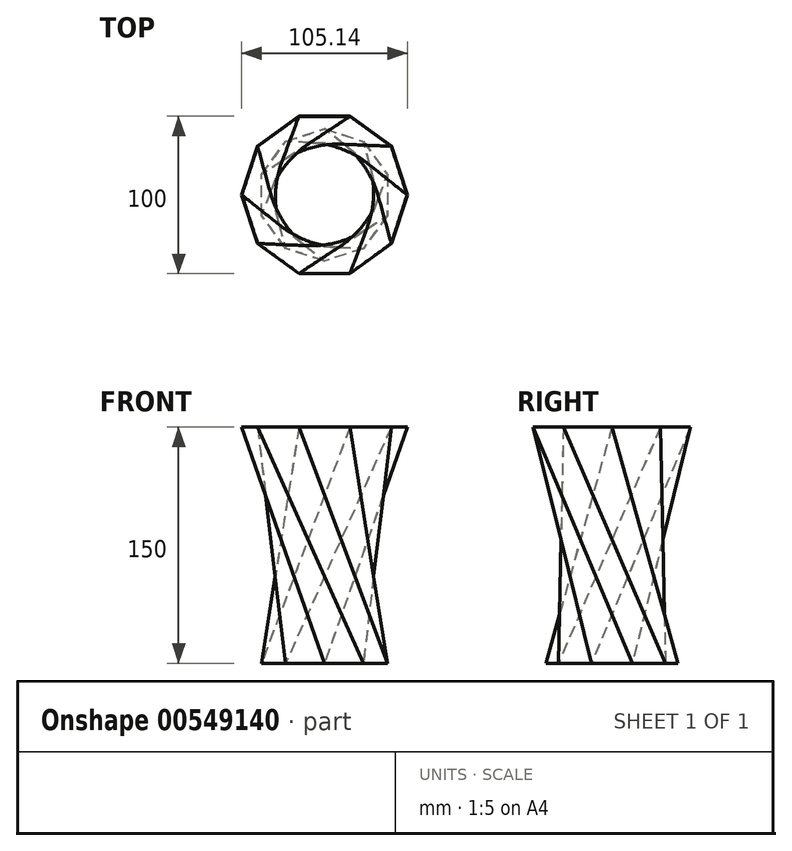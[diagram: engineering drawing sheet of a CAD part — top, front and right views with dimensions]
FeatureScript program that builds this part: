
annotation { "Feature Type Name" : "Feature", "Feature Type Description" : "" }
export const myFeature = defineFeature(function(context is Context, id is Id, definition is map)
    precondition{}
    {
        {
            var Q0;
            Q0=qCreatedBy(makeId("Top.planeOp"),FACE);
            var sketch = newSketch(context, id + "F0", { "sketchPlane" : qUnion([Q0])});
            skCircle(sketch, "E0.cCircle", {"center": v(0, 0) * mm, "radius": 40 * mm, "construction": true});
            skLineSegment(sketch, "E0.0", {"start": v(0, 42.06) * mm, "end": v(24.72, 34.03) * mm});
            skLineSegment(sketch, "E0.1", {"start": v(24.72, 34.03) * mm, "end": v(40, 13) * mm});
            skLineSegment(sketch, "E0.2", {"start": v(40, 13) * mm, "end": v(40, -13) * mm});
            skLineSegment(sketch, "E0.3", {"start": v(40, -13) * mm, "end": v(24.72, -34.03) * mm});
            skLineSegment(sketch, "E0.4", {"start": v(24.72, -34.03) * mm, "end": v(0, -42.06) * mm});
            skLineSegment(sketch, "E0.5", {"start": v(0, -42.06) * mm, "end": v(-24.72, -34.03) * mm});
            skLineSegment(sketch, "E0.6", {"start": v(-24.72, -34.03) * mm, "end": v(-40, -13) * mm});
            skLineSegment(sketch, "E0.7", {"start": v(-40, -13) * mm, "end": v(-40, 13) * mm});
            skLineSegment(sketch, "E0.8", {"start": v(-40, 13) * mm, "end": v(-24.72, 34.03) * mm});
            skLineSegment(sketch, "E0.9", {"start": v(-24.72, 34.03) * mm, "end": v(0, 42.06) * mm});
            skPoint(sketch, "E0.0.midPoint", {"position": v(12.36, 38.04) * mm});
            skLineSegment(sketch, "E1", {"start": v(0, 40) * mm, "end": v(24.72, 42.06) * mm, "construction": true});
            skLineSegment(sketch, "E2", {"start": v(24.72, 42.06) * mm, "end": v(25.67, 30.68) * mm, "construction": true});
            skSolve(sketch);
        }
        {
            var Q0;
            Q0=qCreatedBy(makeId("Top.planeOp"),FACE);
            cPlane(context, id + "F1", {"entities" : qUnion([Q0]), "cplaneType" : CPlaneType.OFFSET, "offset" : 150 * mm, "width" : 152.4 * mm, "height" : 152.4 * mm});
        }
        {
            var Q0;
            Q0=qCreatedBy(id+"F1.planeOp",FACE);
            var sketch = newSketch(context, id + "F2", { "sketchPlane" : qUnion([Q0])});
            skCircle(sketch, "E3.cCircle", {"center": v(0, 0) * mm, "radius": 50 * mm, "construction": true});
            skLineSegment(sketch, "E3.0", {"start": v(42.53, 30.9) * mm, "end": v(52.57, 0) * mm});
            skLineSegment(sketch, "E3.1", {"start": v(52.57, 0) * mm, "end": v(42.53, -30.9) * mm});
            skLineSegment(sketch, "E3.2", {"start": v(42.53, -30.9) * mm, "end": v(16.25, -50) * mm});
            skLineSegment(sketch, "E3.3", {"start": v(16.25, -50) * mm, "end": v(-16.25, -50) * mm});
            skLineSegment(sketch, "E3.4", {"start": v(-16.25, -50) * mm, "end": v(-42.53, -30.9) * mm});
            skLineSegment(sketch, "E3.5", {"start": v(-42.53, -30.9) * mm, "end": v(-52.57, 0) * mm});
            skLineSegment(sketch, "E3.6", {"start": v(-52.57, 0) * mm, "end": v(-42.53, 30.9) * mm});
            skLineSegment(sketch, "E3.7", {"start": v(-42.53, 30.9) * mm, "end": v(-16.25, 50) * mm});
            skLineSegment(sketch, "E3.8", {"start": v(-16.25, 50) * mm, "end": v(16.25, 50) * mm});
            skLineSegment(sketch, "E3.9", {"start": v(16.25, 50) * mm, "end": v(42.53, 30.9) * mm});
            skPoint(sketch, "E3.0.midPoint", {"position": v(47.55, 15.45) * mm});
            skPoint(sketch, "E4", {"position": v(0, 50) * mm});
            skSolve(sketch);
        }
        {
            var Q0;
            Q0=makeQuery(id+"F2.imprint","IMPRINT",FACE,{"disambiguationData":[TD([[makeQuery(id+"F2.imprint","IMPRINT",EDGE,{"derivedFrom":sQuery(id+"F2.wireOp",EDGE,"E3.0")}),-1.0]])]});
            var Q1;
            Q1 = qSketchRegion(id + "F0", true);
            var Q2;
            Q2=sQuery(id+"F0.wireOp",VERTEX,"E0.3.end");
            var Q3;
            Q3=sQuery(id+"F2.wireOp",VERTEX,"E3.4.end");
            loft(context, id + "F3", {"sheetProfilesArray" : [{ "sheetProfileEntities" : qUnion([Q0]) }, { "sheetProfileEntities" : qUnion([Q1]) }], "matchConnections" : true, "connections" : [{ "connectionEntities" : qUnion([Q2, Q3]), "connectionEdgeQueries" : qUnion([]), "connectionEdgeParameters" : [] }]});
        }
        {
            var Q0;
            Q0=makeQuery(id+"F3.opLoft","CAP_FACE",FACE,{"disambiguationData":[OSD([makeQuery(id+"F2.imprint","IMPRINT",FACE,{"disambiguationData":[TD([[makeQuery(id+"F2.imprint","IMPRINT",EDGE,{"derivedFrom":sQuery(id+"F2.wireOp",EDGE,"E3.0")}),-1.0]])]})])],"isStart":true});
            shell(context, id + "F4", {"entities" : qUnion([Q0]), "thickness" : 0.1 * mm});
        }
    });
